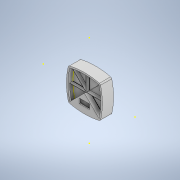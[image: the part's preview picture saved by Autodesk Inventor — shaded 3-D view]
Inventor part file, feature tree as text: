
AUTODESK INVENTOR PART (.ipt)
format: ipt  version: 2021 (Build 250183000, 183)  size: 303,104 bytes
history: native  units: mm
features: sketch x10, extrude x9, other x1, fillet x1, shell x1, projected_geometry x1
ambient origin geometry x8: Origin, YZ Plane, XZ Plane, XY Plane, X Axis, Y Axis, Z Axis, Center Point
bodies: Body1 (feature_tree)
feature tree (23):
  other  "Sólido1"
  extrude  "Extrusión1"  Depth=400.0mm
  fillet  "Empalme1"  Radius=400.0mm
  extrude  "Extrusión2"  Depth=400.0mm
  sketch  "Boceto 3D3"  dims[d5=400.0mm d6=40.0mm d7=0.0mm]
  extrude  "Extrusión3"  Depth=40.0mm TaperAngle=0.0deg
  extrude  "Extrusión4"  Depth=30.0mm TaperAngle=0.0deg
  extrude  "Extrusión5"  Depth=30.0mm TaperAngle=0.0deg
  extrude  "Extrusión6"  Depth=3.0mm
  extrude  "Extrusión7"  Depth=30.0mm TaperAngle=0.0deg
  sketch  "Boceto23"  dims[d24=65.0mm d25=5.0mm d26=0.0mm]
  extrude  "Extrusión14"  Depth=5.0mm TaperAngle=0.0deg
  extrude  "Extrusión15"  Depth=4.0mm
  shell  "Vaciado7"  Thickness=4.0mm
  sketch  "Boceto1"  dims[d0=200.0mm d1=200.0mm d2=400.0mm]
  sketch  "Boceto2"  dims[d3=400.0mm d4=400.0mm]
  sketch  "Boceto5"  dims[d8=10.0mm d11=30.0mm d12=0.0mm]
  projected_geometry  "Contorno proyectado1"
  sketch  "Boceto9"  dims[d13=30.0mm d14=0.0mm d15=30.0mm d16=0.0mm]
  sketch  "Boceto11"  dims[d17=35.0mm d18=0.0mm d19=3.0mm]
  sketch  "Boceto12"  dims[d20=3.0mm d21=30.0mm d22=0.0mm]
  sketch  "Boceto33"  dims[d46=4.0mm d48=4.0mm d50=4.0mm]
  sketch  "Boceto34"  dims[d52=4.0mm d53=4.0mm d54=0.0mm d55=20.0mm d56=0.0mm d57=2.0mm d27=0.5mm d28=0.872665mm d29=0.5mm d30=0.872665mm d33=0.5mm d34=0.872665mm d35=0.5mm d36=0.872665mm d39=0.5mm d40=0.872665mm d41=0.5mm d42=0.872665mm d58=0.872665mm d59=0.872665mm d60=0.5mm d61=0.872665mm]
